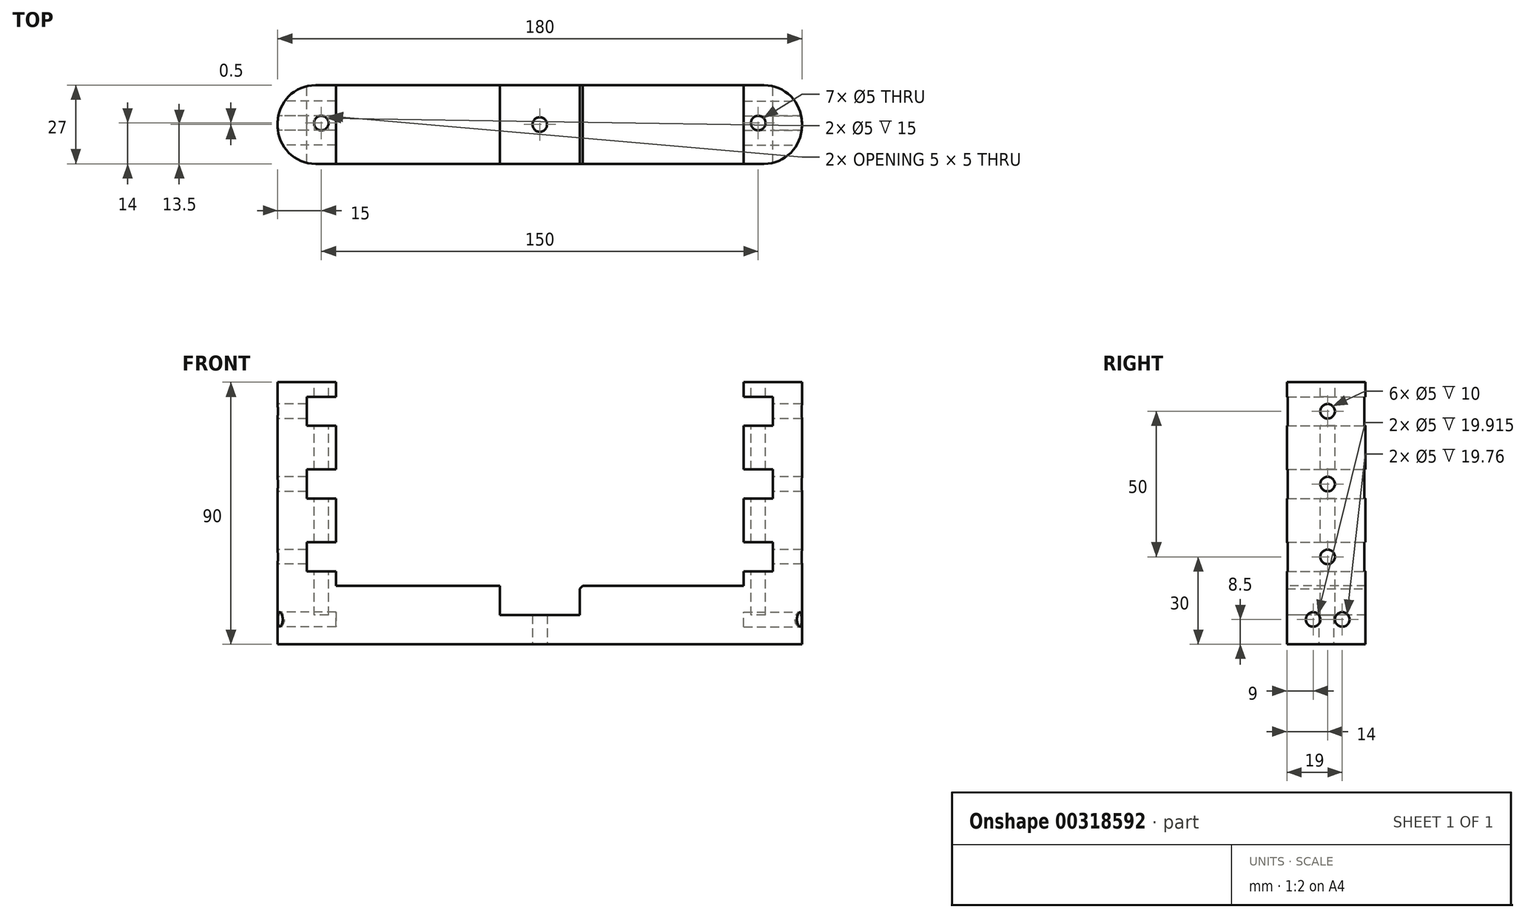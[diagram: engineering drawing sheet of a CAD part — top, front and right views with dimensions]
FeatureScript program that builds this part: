
annotation { "Feature Type Name" : "Feature", "Feature Type Description" : "" }
export const myFeature = defineFeature(function(context is Context, id is Id, definition is map)
    precondition{}
    {
        {
            var Q0;
            Q0=qCreatedBy(makeId("Front.planeOp"),FACE);
            var sketch = newSketch(context, id + "F0", { "sketchPlane" : qUnion([Q0])});
            skLineSegment(sketch, "E0.bottom", {"start": v(0, 0) * mm, "end": v(180, 0) * mm});
            skLineSegment(sketch, "E0.top", {"start": v(0, 90) * mm, "end": v(180, 90) * mm});
            skLineSegment(sketch, "E0.left", {"start": v(0, 0) * mm, "end": v(0, 90) * mm});
            skLineSegment(sketch, "E0.right", {"start": v(180, 0) * mm, "end": v(180, 90) * mm});
            skSolve(sketch);
        }
        {
            var Q0;
            Q0=makeQuery(id+"F0.imprint","IMPRINT",FACE,{"disambiguationData":[TD([[makeQuery(id+"F0.imprint","IMPRINT",EDGE,{"derivedFrom":sQuery(id+"F0.wireOp",EDGE,"E0.bottom")}),1.0]])]});
            extrude(context, id + "F1", {"entities" : qUnion([Q0]), "depth" : 27 * mm});
        }
        {
            var Q0;
            Q0=qCreatedBy(makeId("Front.planeOp"),FACE);
            var sketch = newSketch(context, id + "F2", { "sketchPlane" : qUnion([Q0])});
            skLineSegment(sketch, "E1.bottom", {"start": v(20, 90) * mm, "end": v(160, 90) * mm});
            skLineSegment(sketch, "E1.top", {"start": v(20, 20) * mm, "end": v(160, 20) * mm});
            skLineSegment(sketch, "E1.left", {"start": v(20, 90) * mm, "end": v(20, 20) * mm});
            skLineSegment(sketch, "E1.right", {"start": v(160, 90) * mm, "end": v(160, 20) * mm});
            skSolve(sketch);
        }
        {
            var Q0;
            Q0=makeQuery(id+"F2.imprint","IMPRINT",FACE,{"disambiguationData":[TD([[makeQuery(id+"F2.imprint","IMPRINT",EDGE,{"derivedFrom":sQuery(id+"F2.wireOp",EDGE,"E1.bottom")}),-1.0]])]});
            extrude(context, id + "F3", {"entities" : qUnion([Q0]), "operationType" : NewBodyOperationType.REMOVE, "endBound" : BoundingType.THROUGH_ALL, "depth" : 25 * mm});
        }
        {
            var Q0;
            Q0=qCreatedBy(makeId("Front.planeOp"),FACE);
            var sketch = newSketch(context, id + "F4", { "sketchPlane" : qUnion([Q0])});
            skLineSegment(sketch, "E2.bottom", {"start": v(170, 85) * mm, "end": v(160, 85) * mm});
            skLineSegment(sketch, "E2.top", {"start": v(170, 75) * mm, "end": v(160, 75) * mm});
            skLineSegment(sketch, "E2.left", {"start": v(170, 85) * mm, "end": v(170, 75) * mm});
            skLineSegment(sketch, "E2.right", {"start": v(160, 85) * mm, "end": v(160, 75) * mm});
            skLineSegment(sketch, "E3.bottom", {"start": v(170, 60) * mm, "end": v(160, 60) * mm});
            skLineSegment(sketch, "E3.top", {"start": v(170, 50) * mm, "end": v(160, 50) * mm});
            skLineSegment(sketch, "E3.left", {"start": v(170, 60) * mm, "end": v(170, 50) * mm});
            skLineSegment(sketch, "E3.right", {"start": v(160, 60) * mm, "end": v(160, 50) * mm});
            skLineSegment(sketch, "E4.bottom", {"start": v(170, 35) * mm, "end": v(160, 35) * mm});
            skLineSegment(sketch, "E4.top", {"start": v(170, 25) * mm, "end": v(160, 25) * mm});
            skLineSegment(sketch, "E4.left", {"start": v(170, 35) * mm, "end": v(170, 25) * mm});
            skLineSegment(sketch, "E4.right", {"start": v(160, 35) * mm, "end": v(160, 25) * mm});
            skLineSegment(sketch, "E5.bottom", {"start": v(20, 85) * mm, "end": v(10, 85) * mm});
            skLineSegment(sketch, "E5.top", {"start": v(20, 75) * mm, "end": v(10, 75) * mm});
            skLineSegment(sketch, "E5.left", {"start": v(20, 85) * mm, "end": v(20, 75) * mm});
            skLineSegment(sketch, "E5.right", {"start": v(10, 85) * mm, "end": v(10, 75) * mm});
            skLineSegment(sketch, "E6.bottom", {"start": v(20, 60) * mm, "end": v(10, 60) * mm});
            skLineSegment(sketch, "E6.top", {"start": v(20, 50) * mm, "end": v(10, 50) * mm});
            skLineSegment(sketch, "E6.left", {"start": v(20, 60) * mm, "end": v(20, 50) * mm});
            skLineSegment(sketch, "E6.right", {"start": v(10, 60) * mm, "end": v(10, 50) * mm});
            skLineSegment(sketch, "E7.bottom", {"start": v(20, 35) * mm, "end": v(10, 35) * mm});
            skLineSegment(sketch, "E7.top", {"start": v(20, 25) * mm, "end": v(10, 25) * mm});
            skLineSegment(sketch, "E7.left", {"start": v(20, 35) * mm, "end": v(20, 25) * mm});
            skLineSegment(sketch, "E7.right", {"start": v(10, 35) * mm, "end": v(10, 25) * mm});
            skLineSegment(sketch, "E8", {"start": v(170, 90) * mm, "end": v(170, 40) * mm, "construction": true});
            skLineSegment(sketch, "E9", {"start": v(10, 90) * mm, "end": v(10, 85) * mm, "construction": true});
            skSolve(sketch);
        }
        {
            var Q0;
            Q0=makeQuery(id+"F4.imprint","IMPRINT",FACE,{"disambiguationData":[TD([[makeQuery(id+"F4.imprint","IMPRINT",EDGE,{"derivedFrom":sQuery(id+"F4.wireOp",EDGE,"E2.bottom")}),1.0]])]});
            var Q1;
            Q1=makeQuery(id+"F4.imprint","IMPRINT",FACE,{"disambiguationData":[TD([[makeQuery(id+"F4.imprint","IMPRINT",EDGE,{"derivedFrom":sQuery(id+"F4.wireOp",EDGE,"E3.bottom")}),1.0]])]});
            var Q2;
            Q2=makeQuery(id+"F4.imprint","IMPRINT",FACE,{"disambiguationData":[TD([[makeQuery(id+"F4.imprint","IMPRINT",EDGE,{"derivedFrom":sQuery(id+"F4.wireOp",EDGE,"E4.bottom")}),1.0]])]});
            var Q3;
            Q3=makeQuery(id+"F4.imprint","IMPRINT",FACE,{"disambiguationData":[TD([[makeQuery(id+"F4.imprint","IMPRINT",EDGE,{"derivedFrom":sQuery(id+"F4.wireOp",EDGE,"E7.bottom")}),1.0]])]});
            var Q4;
            Q4=makeQuery(id+"F4.imprint","IMPRINT",FACE,{"disambiguationData":[TD([[makeQuery(id+"F4.imprint","IMPRINT",EDGE,{"derivedFrom":sQuery(id+"F4.wireOp",EDGE,"E6.bottom")}),1.0]])]});
            var Q5;
            Q5=makeQuery(id+"F4.imprint","IMPRINT",FACE,{"disambiguationData":[TD([[makeQuery(id+"F4.imprint","IMPRINT",EDGE,{"derivedFrom":sQuery(id+"F4.wireOp",EDGE,"E5.bottom")}),1.0]])]});
            extrude(context, id + "F5", {"entities" : qUnion([Q0, Q1, Q2, Q3, Q4, Q5]), "operationType" : NewBodyOperationType.REMOVE, "endBound" : BoundingType.THROUGH_ALL, "depth" : 25 * mm});
        }
        {
            var Q0;
            {var subQ0=sQuery(id+"F0.wireOp",EDGE,"E0.right");var subQ2=sQuery(id+"F0.wireOp",EDGE,"E0.top");Q0=makeQuery(id+"F3.boolean.opBoolean","SPLIT",FACE,{"disambiguationData":[TD([makeQuery(id+"F1.opExtrude","SWEPT_FACE",FACE,{"disambiguationData":[OSD([subQ0])]})])],"derivedFrom":makeQuery(id+"F1.opExtrude","SWEPT_FACE",FACE,{"disambiguationData":[OSD([subQ2])]})});}
            var sketch = newSketch(context, id + "F6", { "sketchPlane" : qUnion([Q0])});
            skCircle(sketch, "E10", {"center": v(165, -13) * mm, "radius": 2.5 * mm});
            skCircle(sketch, "E11", {"center": v(15, -13) * mm, "radius": 2.5 * mm});
            skLineSegment(sketch, "E12", {"start": v(90, 0) * mm, "end": v(90, -27) * mm, "construction": true});
            skSolve(sketch);
        }
        {
            var Q0;
            Q0=makeQuery(id+"F6.imprint","IMPRINT",FACE,{"disambiguationData":[TD([[makeQuery(id+"F6.imprint","IMPRINT",EDGE,{"derivedFrom":sQuery(id+"F6.wireOp",EDGE,"E10")}),1.0]])]});
            var Q1;
            Q1=makeQuery(id+"F6.imprint","IMPRINT",FACE,{"disambiguationData":[TD([[makeQuery(id+"F6.imprint","IMPRINT",EDGE,{"derivedFrom":sQuery(id+"F6.wireOp",EDGE,"E11")}),1.0]])]});
            extrude(context, id + "F7", {"entities" : qUnion([Q0, Q1]), "operationType" : NewBodyOperationType.REMOVE, "oppositeDirection" : true, "depth" : 80 * mm});
        }
        {
            var Q0;
            Q0=qCreatedBy(makeId("Right.planeOp"),FACE);
            var sketch = newSketch(context, id + "F8", { "sketchPlane" : qUnion([Q0])});
            skCircle(sketch, "E13", {"center": v(-13, 80) * mm, "radius": 2.5 * mm});
            skCircle(sketch, "E14", {"center": v(-13, 55) * mm, "radius": 2.5 * mm});
            skCircle(sketch, "E15", {"center": v(-13, 30) * mm, "radius": 2.5 * mm});
            skLineSegment(sketch, "E16", {"start": v(-27, 30) * mm, "end": v(0, 30) * mm, "construction": true});
            skLineSegment(sketch, "E17", {"start": v(-27, 55) * mm, "end": v(0, 55) * mm, "construction": true});
            skLineSegment(sketch, "E18", {"start": v(-13, 0) * mm, "end": v(-13, 90) * mm});
            skSolve(sketch);
        }
        {
            var Q0;
            Q0=makeQuery(id+"F8.imprint","IMPRINT",FACE,{"disambiguationData":[TD([[makeQuery(id+"F8.imprint","IMPRINT",EDGE,{"derivedFrom":sQuery(id+"F8.wireOp",EDGE,"E13")}),1.0]])]});
            var Q1;
            Q1=makeQuery(id+"F8.imprint","IMPRINT",FACE,{"disambiguationData":[TD([[makeQuery(id+"F8.imprint","IMPRINT",EDGE,{"derivedFrom":sQuery(id+"F8.wireOp",EDGE,"E14")}),1.0]])]});
            var Q2;
            Q2=makeQuery(id+"F8.imprint","IMPRINT",FACE,{"disambiguationData":[TD([[makeQuery(id+"F8.imprint","IMPRINT",EDGE,{"derivedFrom":sQuery(id+"F8.wireOp",EDGE,"E15")}),1.0]])]});
            extrude(context, id + "F9", {"entities" : qUnion([Q0, Q1, Q2]), "operationType" : NewBodyOperationType.REMOVE, "endBound" : BoundingType.THROUGH_ALL, "depth" : 25 * mm});
        }
        {
            var Q0;
            Q0=qCreatedBy(makeId("Right.planeOp"),FACE);
            var sketch = newSketch(context, id + "F10", { "sketchPlane" : qUnion([Q0])});
            skCircle(sketch, "E19", {"center": v(-8, 8.5) * mm, "radius": 2.5 * mm});
            skCircle(sketch, "E20", {"center": v(-18, 8.5) * mm, "radius": 2.5 * mm});
            skSolve(sketch);
        }
        {
            var Q0;
            Q0=makeQuery(id+"F1.opExtrude","SWEPT_FACE",FACE,{"disambiguationData":[OSD([sQuery(id+"F0.wireOp",EDGE,"E0.right")])]});
            var sketch = newSketch(context, id + "F11", { "sketchPlane" : qUnion([Q0])});
            skCircle(sketch, "E21", {"center": v(-18, 8.5) * mm, "radius": 2.5 * mm});
            skCircle(sketch, "E22", {"center": v(-8, 8.5) * mm, "radius": 2.5 * mm});
            skSolve(sketch);
        }
        {
            var Q0;
            Q0=makeQuery(id+"F11.imprint","IMPRINT",FACE,{"disambiguationData":[TD([[makeQuery(id+"F11.imprint","IMPRINT",EDGE,{"derivedFrom":sQuery(id+"F11.wireOp",EDGE,"E22")}),1.0]])]});
            var Q1;
            Q1=makeQuery(id+"F11.imprint","IMPRINT",FACE,{"disambiguationData":[TD([[makeQuery(id+"F11.imprint","IMPRINT",EDGE,{"derivedFrom":sQuery(id+"F11.wireOp",EDGE,"E21")}),1.0]])]});
            extrude(context, id + "F12", {"entities" : qUnion([Q0, Q1]), "operationType" : NewBodyOperationType.REMOVE, "oppositeDirection" : true, "depth" : 20 * mm});
        }
        {
            var Q0;
            Q0=makeQuery(id+"F10.imprint","IMPRINT",FACE,{"disambiguationData":[TD([[makeQuery(id+"F10.imprint","IMPRINT",EDGE,{"derivedFrom":sQuery(id+"F10.wireOp",EDGE,"E19")}),1.0]])]});
            var Q1;
            Q1=makeQuery(id+"F10.imprint","IMPRINT",FACE,{"disambiguationData":[TD([[makeQuery(id+"F10.imprint","IMPRINT",EDGE,{"derivedFrom":sQuery(id+"F10.wireOp",EDGE,"E20")}),1.0]])]});
            extrude(context, id + "F13", {"entities" : qUnion([Q0, Q1]), "operationType" : NewBodyOperationType.REMOVE, "depth" : 20 * mm});
        }
        {
            var Q0;
            Q0=makeQuery(id+"F1.opExtrude","CAP_EDGE",EDGE,{"disambiguationData":[OSD([sQuery(id+"F0.wireOp",EDGE,"E0.left")])],"isStart":true});
            var Q1;
            Q1=makeQuery(id+"F1.opExtrude","CAP_EDGE",EDGE,{"disambiguationData":[OSD([sQuery(id+"F0.wireOp",EDGE,"E0.left")])],"isStart":false});
            var Q2;
            Q2=makeQuery(id+"F1.opExtrude","CAP_EDGE",EDGE,{"disambiguationData":[OSD([sQuery(id+"F0.wireOp",EDGE,"E0.right")])],"isStart":false});
            var Q3;
            Q3=makeQuery(id+"F1.opExtrude","CAP_EDGE",EDGE,{"disambiguationData":[OSD([sQuery(id+"F0.wireOp",EDGE,"E0.right")])],"isStart":true});
            fillet(context, id + "F14", {"entities" : qUnion([Q0, Q1, Q2, Q3]), "radius" : 13 * mm, "tangentPropagation" : true, "allowEdgeOverflow" : false});
        }
        {
            var Q0;
            Q0=makeQuery(id+"F14.opFillet","SPLIT",FACE,{"disambiguationData":[OD(6.0)],"derivedFrom":makeQuery(id+"F1.opExtrude","CAP_FACE",FACE,{"disambiguationData":[OSD([sQuery(id+"F0.wireOp",EDGE,"E0.bottom"),sQuery(id+"F0.wireOp",EDGE,"E0.top"),sQuery(id+"F0.wireOp",EDGE,"E0.left"),sQuery(id+"F0.wireOp",EDGE,"E0.right")])],"isStart":false})});
            var sketch = newSketch(context, id + "F15", { "sketchPlane" : qUnion([Q0])});
            skLineSegment(sketch, "E23", {"start": v(76.25, 20) * mm, "end": v(76.25, 10) * mm});
            skLineSegment(sketch, "E24", {"start": v(76.25, 10) * mm, "end": v(103.75, 10) * mm});
            skLineSegment(sketch, "E25", {"start": v(103.75, 10) * mm, "end": v(103.75, 20) * mm});
            skSolve(sketch);
        }
        {
            var Q0;
            {var subQ0=sQuery(id+"F15.wireOp",EDGE,"E23");Q0=makeQuery(id+"F15.imprint","IMPRINT",FACE,{"disambiguationData":[TD([[makeQuery(id+"F15.imprint","IMPRINT",EDGE,{"derivedFrom":subQ0}),1.0]])]});}
            extrude(context, id + "F16", {"entities" : qUnion([Q0]), "operationType" : NewBodyOperationType.REMOVE, "endBound" : BoundingType.THROUGH_ALL, "oppositeDirection" : true, "depth" : 25 * mm});
        }
        {
            var Q0;
            Q0=makeQuery(id+"F16.boolean.opBoolean","COPY",FACE,{"derivedFrom":makeQuery(id+"F16.opExtrude","SWEPT_FACE",FACE,{"disambiguationData":[OSD([sQuery(id+"F15.wireOp",EDGE,"E24")])]})});
            var sketch = newSketch(context, id + "F17", { "sketchPlane" : qUnion([Q0])});
            skCircle(sketch, "E26", {"center": v(90, -13.5) * mm, "radius": 2.5 * mm});
            skLineSegment(sketch, "E27", {"start": v(0, -13) * mm, "end": v(180, -14) * mm, "construction": true});
            skSolve(sketch);
        }
        {
            var Q0;
            Q0=makeQuery(id+"F16.boolean.opBoolean","COPY",EDGE,{"derivedFrom":makeQuery(id+"F16.opExtrude","SWEPT_EDGE",EDGE,{"disambiguationData":[OSD([sQuery(id+"F0.wireOp",EDGE,"E0.bottom"),sQuery(id+"F0.wireOp",EDGE,"E0.top"),sQuery(id+"F0.wireOp",EDGE,"E0.left"),sQuery(id+"F0.wireOp",EDGE,"E0.right"),sQuery(id+"F2.wireOp",EDGE,"E1.top"),sQuery(id+"F15.wireOp",EDGE,"E25")])]})});
            var Q1;
            Q1=makeQuery(id+"F16.boolean.opBoolean","COPY",EDGE,{"derivedFrom":makeQuery(id+"F16.opExtrude","SWEPT_EDGE",EDGE,{"disambiguationData":[OSD([sQuery(id+"F0.wireOp",EDGE,"E0.bottom"),sQuery(id+"F0.wireOp",EDGE,"E0.top"),sQuery(id+"F0.wireOp",EDGE,"E0.left"),sQuery(id+"F0.wireOp",EDGE,"E0.right"),sQuery(id+"F2.wireOp",EDGE,"E1.top"),sQuery(id+"F15.wireOp",EDGE,"E23")])]})});
            chamfer(context, id + "F18", {"entities" : qUnion([Q0, Q1]), "width" : 1 * mm, "tangentPropagation" : true});
        }
        {
            var Q0;
            Q0=makeQuery(id+"F1.opExtrude","SWEPT_FACE",FACE,{"disambiguationData":[OSD([sQuery(id+"F0.wireOp",EDGE,"E0.bottom")])]});
            var sketch = newSketch(context, id + "F19", { "sketchPlane" : qUnion([Q0])});
            skCircle(sketch, "E28", {"center": v(90, 13.5) * mm, "radius": 2.5 * mm});
            skSolve(sketch);
        }
        {
            var Q0;
            Q0=makeQuery(id+"F19.imprint","IMPRINT",FACE,{"disambiguationData":[TD([[makeQuery(id+"F19.imprint","IMPRINT",EDGE,{"derivedFrom":sQuery(id+"F19.wireOp",EDGE,"E28")}),1.0]])]});
            extrude(context, id + "F20", {"entities" : qUnion([Q0]), "operationType" : NewBodyOperationType.REMOVE, "endBound" : BoundingType.THROUGH_ALL, "oppositeDirection" : true, "depth" : 25 * mm});
        }
    });
